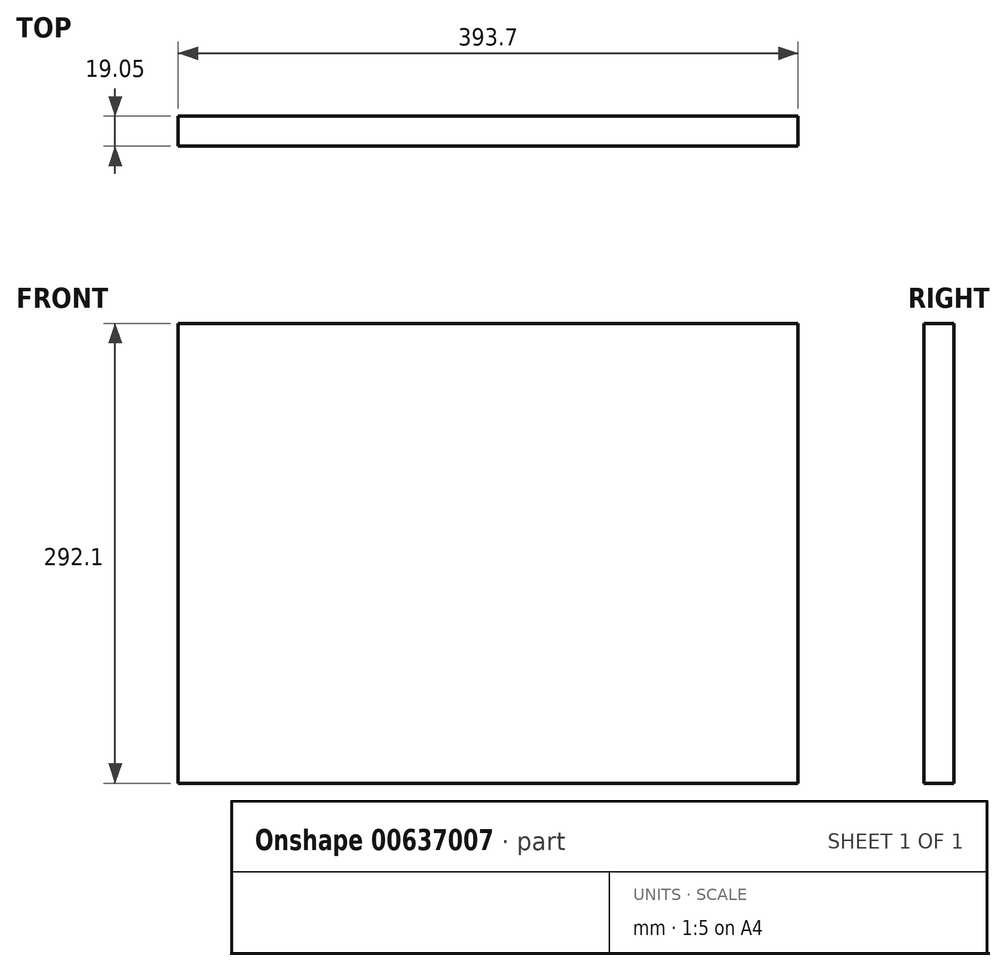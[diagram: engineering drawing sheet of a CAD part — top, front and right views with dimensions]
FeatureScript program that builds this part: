
annotation { "Feature Type Name" : "Feature", "Feature Type Description" : "" }
export const myFeature = defineFeature(function(context is Context, id is Id, definition is map)
    precondition{}
    {
        {
            var Q0;
            Q0=qCreatedBy(makeId("Front.planeOp"),FACE);
            var sketch = newSketch(context, id + "F0", { "sketchPlane" : qUnion([Q0])});
            skLineSegment(sketch, "E0.bottom", {"start": v(196.85, 146.05) * mm, "end": v(-196.85, 146.05) * mm});
            skLineSegment(sketch, "E0.top", {"start": v(196.85, -146.05) * mm, "end": v(-196.85, -146.05) * mm});
            skLineSegment(sketch, "E0.left", {"start": v(196.85, 146.05) * mm, "end": v(196.85, -146.05) * mm});
            skLineSegment(sketch, "E0.right", {"start": v(-196.85, 146.05) * mm, "end": v(-196.85, -146.05) * mm});
            skPoint(sketch, "E0.middle", {"position": v(0, 0) * mm});
            skSolve(sketch);
        }
        {
            var Q0;
            Q0=makeQuery(id+"F0.imprint","IMPRINT",FACE,{"disambiguationData":[TD([[makeQuery(id+"F0.imprint","IMPRINT",EDGE,{"derivedFrom":sQuery(id+"F0.wireOp",EDGE,"E0.bottom")}),1.0]])]});
            extrude(context, id + "F1", {"entities" : qUnion([Q0]), "depth" : 19.05 * mm, "offsetDistance" : 25.4 * mm});
        }
    });
